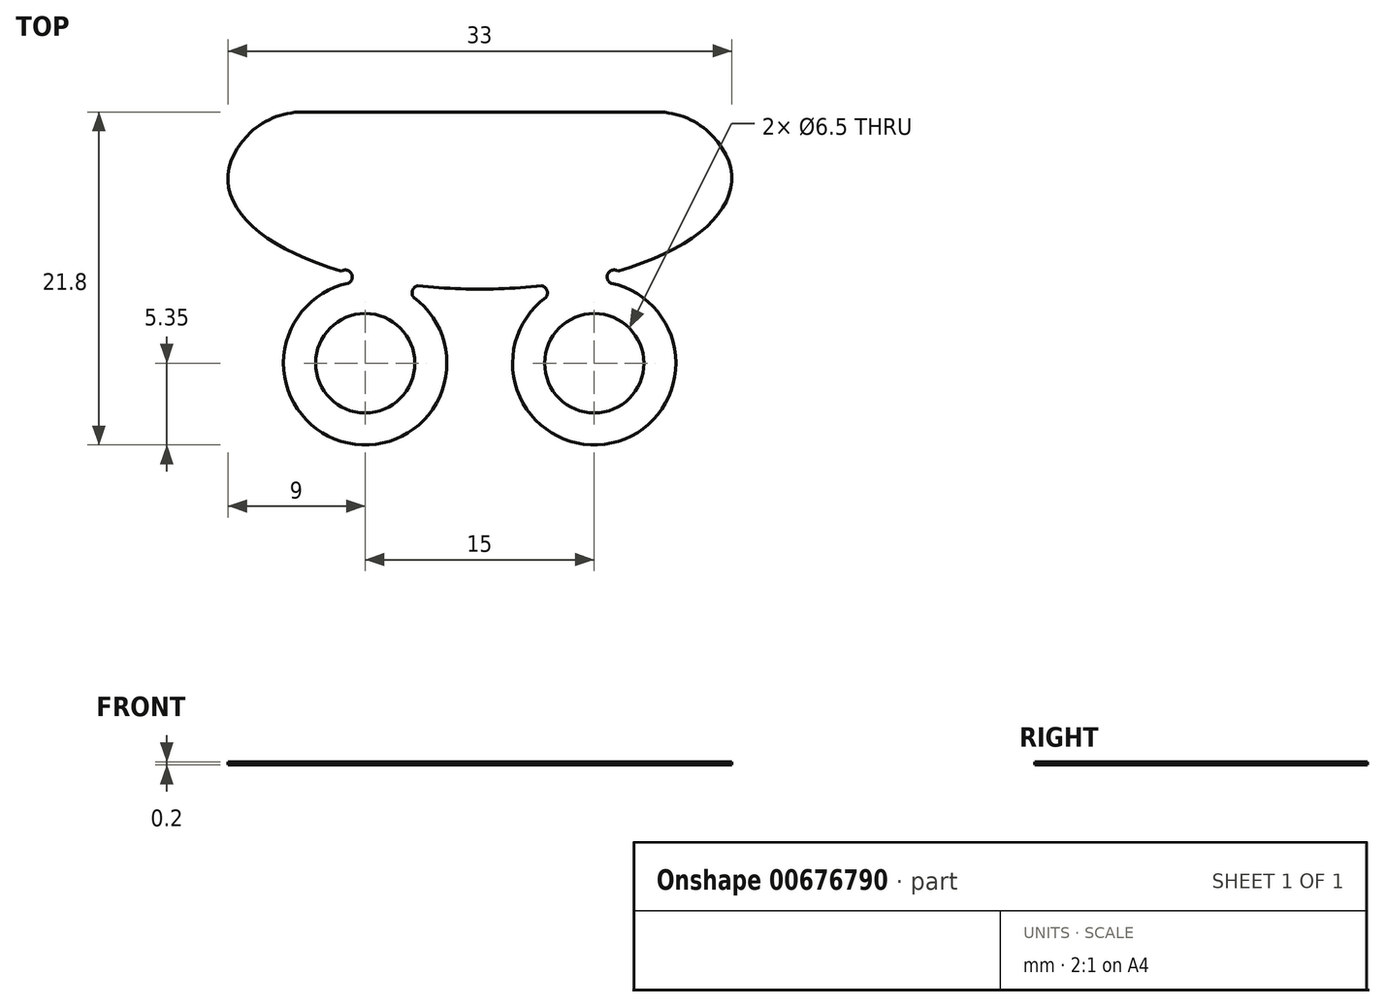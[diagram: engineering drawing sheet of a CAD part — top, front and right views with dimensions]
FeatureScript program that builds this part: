
annotation { "Feature Type Name" : "Feature", "Feature Type Description" : "" }
export const myFeature = defineFeature(function(context is Context, id is Id, definition is map)
    precondition{}
    {
        {
            var Q0;
            Q0=qCreatedBy(makeId("Top.planeOp"),FACE);
            var sketch = newSketch(context, id + "F0", { "sketchPlane" : qUnion([Q0])});
            skLineSegment(sketch, "E0", {"start": v(-13.2, 4.35) * mm, "end": v(13.2, 4.35) * mm});
            skPoint(sketch, "E1", {"position": v(0, -7.25) * mm});
            skCircle(sketch, "E2", {"center": v(-7.5, -12.1) * mm, "radius": 3.25 * mm});
            skLineSegment(sketch, "E3", {"start": v(0, 24.36) * mm, "end": v(0, -25.37) * mm, "construction": true});
            skPoint(sketch, "E4", {"position": v(-7.5, -17.45) * mm});
            skArc(sketch, "E5", {"start": v(-4.06, -7.03) * mm, "mid": v(-4.4, -7.33) * mm, "end": v(-4.33, -7.79) * mm});
            skArc(sketch, "E6", {"start": v(-8.6, -6.86) * mm, "mid": v(-8.4, -6.22) * mm, "end": v(-9.05, -6.06) * mm});
            skEllipticalArc(sketch, "E7", {});
            skEllipticalArc(sketch, "E8", {"construction": true});
            skEllipticalArc(sketch, "E9", {"construction": true});
            skEllipticalArc(sketch, "E10", {});
            skArc(sketch, "E11", {"start": v(-8.6, -6.86) * mm, "mid": v(-8.63, -17.33) * mm, "end": v(-4.33, -7.79) * mm});
            skArc(sketch, "E12", {"start": v(-4.33, -7.79) * mm, "mid": v(-6.37, -6.87) * mm, "end": v(-8.6, -6.86) * mm, "construction": true});
            skArc(sketch, "E13.MirrorCS", {"start": v(4.06, -7.03) * mm, "mid": v(4.4, -7.33) * mm, "end": v(4.33, -7.79) * mm});
            skCircle(sketch, "E14.MirrorC", {"center": v(7.5, -12.1) * mm, "radius": 3.25 * mm});
            skArc(sketch, "E15.MirrorCS", {"start": v(8.6, -6.86) * mm, "mid": v(8.63, -17.33) * mm, "end": v(4.33, -7.79) * mm});
            skArc(sketch, "E16.MirrorCS", {"start": v(8.6, -6.86) * mm, "mid": v(8.4, -6.22) * mm, "end": v(9.05, -6.06) * mm});
            skEllipticalArc(sketch, "E17", {"construction": true});
            skEllipticalArc(sketch, "E18", {});
            const initialGuessF0  = {"E7": [0, 0, 1, 0, 0.0165, 0.00725, 2.49809154479651, 4.131702326846454], "E8": [0, 0, 1, 0, 0.0165, 0.00725, 0.6435011087932834, 2.49809154479651], "E9": [0, 0, 1, 0, 0.0165, 0.00725, 4.131702326846454, 4.4636922706174795], "E10": [0, 0, 1, 0, 0.0165, 0.00725, 4.4636922706174795, 4.961085690151901], "E17": [0, 0, 1, 0, 0.0165, 0.00725, 4.961085690151901, 5.293075633922927], "E18": [0, 0, 1, 0, 0.0165, 0.00725, 5.293075633922927, 0.6435011087932834]};
            skSetInitialGuess(sketch, initialGuessF0);
            skSolve(sketch);
        }
        {
            var Q0;
            Q0=makeQuery(id+"F0.imprint","IMPRINT",FACE,{"disambiguationData":[TD([[makeQuery(id+"F0.imprint","IMPRINT",EDGE,{"derivedFrom":sQuery(id+"F0.wireOp",EDGE,"E0")}),-1.0]])]});
            extrude(context, id + "F1", {"entities" : qUnion([Q0]), "depth" : 0.2 * mm, "offsetDistance" : 25 * mm});
        }
        {
            var Q0;
            Q0=makeQuery(id+"F1.opExtrude","SWEPT_EDGE",EDGE,{"disambiguationData":[OSD([sQuery(id+"F0.wireOp",EDGE,"E0"),sQuery(id+"F0.wireOp",EDGE,"E18")])]});
            var Q1;
            Q1=makeQuery(id+"F1.opExtrude","SWEPT_EDGE",EDGE,{"disambiguationData":[OSD([sQuery(id+"F0.wireOp",EDGE,"E0"),sQuery(id+"F0.wireOp",EDGE,"E7")])]});
            fillet(context, id + "F2", {"entities" : qUnion([Q0, Q1]), "radius" : 5 * mm, "tangentPropagation" : true, "allowEdgeOverflow" : false});
        }
    });
